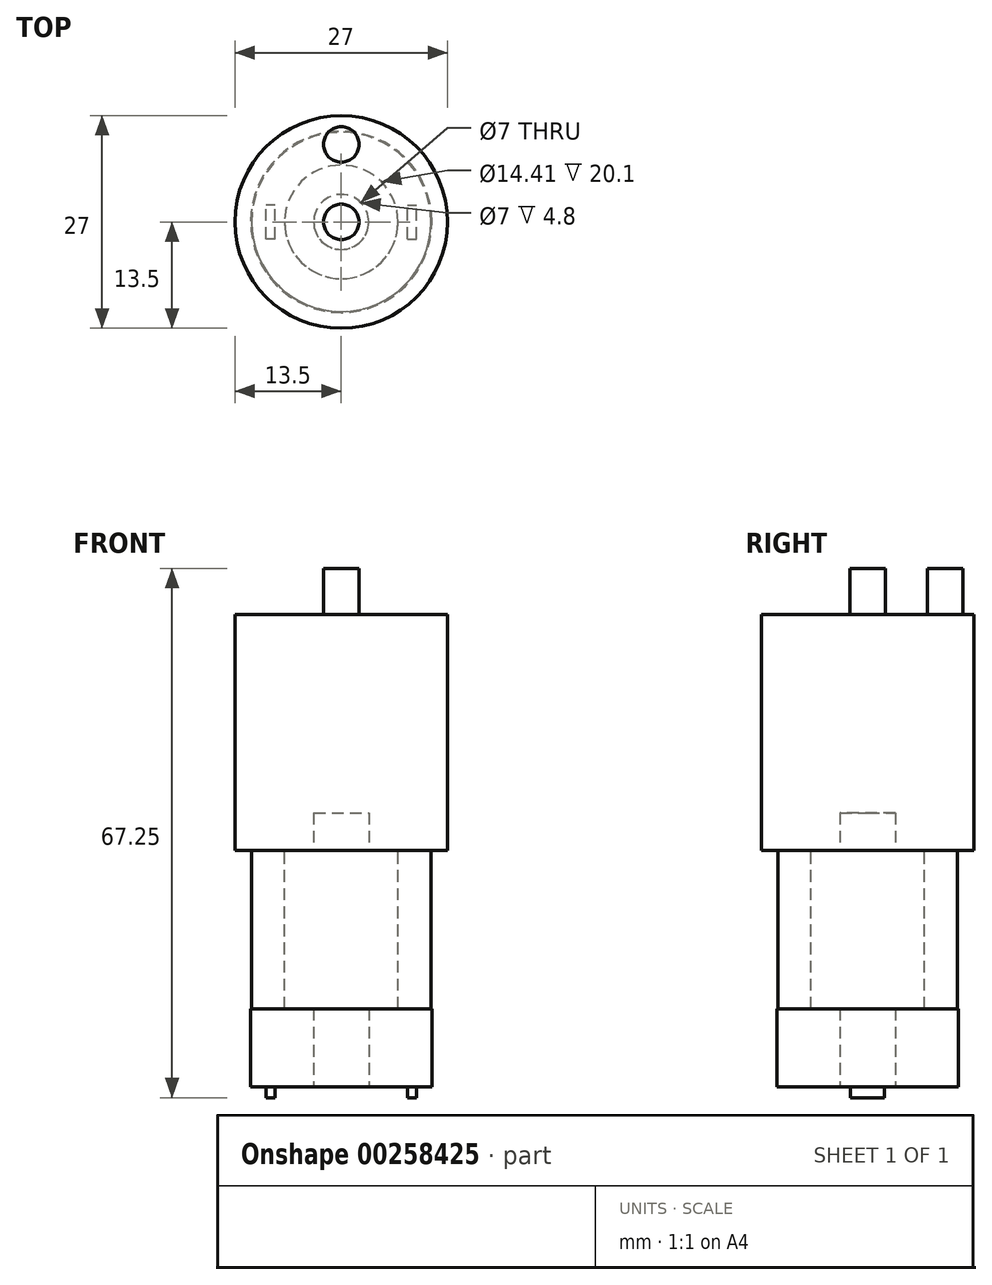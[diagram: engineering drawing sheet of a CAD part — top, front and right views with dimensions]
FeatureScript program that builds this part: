
annotation { "Feature Type Name" : "Feature", "Feature Type Description" : "" }
export const myFeature = defineFeature(function(context is Context, id is Id, definition is map)
    precondition{}
    {
        {
            var Q0;
            Q0=qCreatedBy(makeId("Right.planeOp"),FACE);
            var sketch = newSketch(context, id + "F0", { "sketchPlane" : qUnion([Q0])});
            skLineSegment(sketch, "E0", {"start": v(-11.4, 0) * mm, "end": v(-11.4, 30) * mm});
            skLineSegment(sketch, "E1", {"start": v(-11.4, 30) * mm, "end": v(-7.2, 30) * mm});
            skLineSegment(sketch, "E2", {"start": v(-7.2, 30) * mm, "end": v(-7.2, 0) * mm});
            skLineSegment(sketch, "E3", {"start": v(-7.2, 0) * mm, "end": v(-11.4, 0) * mm});
            skLineSegment(sketch, "E4", {"start": v(0, 33.61) * mm, "end": v(0, -7.5) * mm, "construction": true});
            skLineSegment(sketch, "E5", {"start": v(0, 0) * mm, "end": v(-11.4, 0) * mm, "construction": true});
            skSolve(sketch);
        }
        {
            var Q0;
            Q0=makeQuery(id+"F0.imprint","IMPRINT",FACE,{"disambiguationData":[TD([[makeQuery(id+"F0.imprint","IMPRINT",EDGE,{"derivedFrom":sQuery(id+"F0.wireOp",EDGE,"E0")}),-1.0]])]});
            var Q1;
            Q1=sQuery(id+"F0.wireOp",EDGE,"E4");
            revolve(context, id + "F1", {"entities" : qUnion([Q0]), "axis" : qUnion([Q1]), "revolveType" : RevolveType.FULL});
        }
        {
            var Q0;
            Q0=makeQuery(id+"F1.opRevolve","SWEPT_FACE",FACE,{"disambiguationData":[OSD([sQuery(id+"F0.wireOp",EDGE,"E1")])]});
            var sketch = newSketch(context, id + "F2", { "sketchPlane" : qUnion([Q0])});
            skCircle(sketch, "E6", {"center": v(0, 0) * mm, "radius": 13.5 * mm});
            skSolve(sketch);
        }
        {
            var Q0;
            Q0 = qSketchRegion(id + "F2", true);
            extrude(context, id + "F3", {"entities" : qUnion([Q0]), "operationType" : NewBodyOperationType.ADD, "depth" : 30 * mm});
        }
        {
            var Q0;
            Q0=makeQuery(id+"F1.opRevolve","SWEPT_FACE",FACE,{"disambiguationData":[OSD([sQuery(id+"F0.wireOp",EDGE,"E3")])]});
            var sketch = newSketch(context, id + "F4", { "sketchPlane" : qUnion([Q0])});
            skCircle(sketch, "E7", {"center": v(0, 0) * mm, "radius": 11.5 * mm});
            skSolve(sketch);
        }
        {
            var Q0;
            Q0 = qSketchRegion(id + "F4", true);
            extrude(context, id + "F5", {"entities" : qUnion([Q0]), "operationType" : NewBodyOperationType.ADD, "oppositeDirection" : true, "depth" : 9.9 * mm});
        }
        {
            var Q0;
            Q0=makeQuery(id+"F5.boolean.opBoolean","MERGE",FACE,{"derivedFrom":[makeQuery(id+"F1.opRevolve","SWEPT_FACE",FACE,{"disambiguationData":[OSD([sQuery(id+"F0.wireOp",EDGE,"E3")])]}),makeQuery(id+"F5.opExtrude","CAP_FACE",FACE,{"disambiguationData":[OSD([sQuery(id+"F4.wireOp",EDGE,"E7")])],"isStart":true})]});
            var sketch = newSketch(context, id + "F6", { "sketchPlane" : qUnion([Q0])});
            skCircle(sketch, "E8", {"center": v(0, 0) * mm, "radius": 3.5 * mm});
            skLineSegment(sketch, "E9.bottom", {"start": v(-8.42, 2.15) * mm, "end": v(-9.58, 2.15) * mm});
            skLineSegment(sketch, "E9.top", {"start": v(-8.42, -2.15) * mm, "end": v(-9.58, -2.15) * mm});
            skLineSegment(sketch, "E9.left", {"start": v(-8.42, 2.15) * mm, "end": v(-8.42, -2.15) * mm});
            skLineSegment(sketch, "E9.right", {"start": v(-9.58, 2.15) * mm, "end": v(-9.58, -2.15) * mm});
            skPoint(sketch, "E9.middle", {"position": v(-9, 0) * mm});
            skLineSegment(sketch, "E10", {"start": v(0, -12.15) * mm, "end": v(0, 12.15) * mm, "construction": true});
            skPoint(sketch, "E11.MirrorP", {"position": v(9, 0) * mm});
            skLineSegment(sketch, "E12.MirrorCS", {"start": v(9.58, 2.15) * mm, "end": v(9.58, -2.15) * mm});
            skLineSegment(sketch, "E13.MirrorCS", {"start": v(8.42, 2.15) * mm, "end": v(8.42, -2.15) * mm});
            skLineSegment(sketch, "E14.MirrorCS", {"start": v(8.42, -2.15) * mm, "end": v(9.58, -2.15) * mm});
            skLineSegment(sketch, "E15.MirrorCS", {"start": v(8.42, 2.15) * mm, "end": v(9.58, 2.15) * mm});
            skSolve(sketch);
        }
        {
            var Q0;
            Q0=makeQuery(id+"F6.imprint","IMPRINT",FACE,{"disambiguationData":[TD([[makeQuery(id+"F6.imprint","IMPRINT",EDGE,{"derivedFrom":sQuery(id+"F6.wireOp",EDGE,"E9.bottom")}),1.0]])]});
            var Q1;
            Q1=makeQuery(id+"F6.imprint","IMPRINT",FACE,{"disambiguationData":[TD([[makeQuery(id+"F6.imprint","IMPRINT",EDGE,{"derivedFrom":sQuery(id+"F6.wireOp",EDGE,"E12.MirrorCS")}),-1.0]])]});
            extrude(context, id + "F7", {"entities" : qUnion([Q0, Q1]), "operationType" : NewBodyOperationType.ADD, "depth" : 1.4 * mm});
        }
        {
            var Q0;
            Q0=makeQuery(id+"F6.imprint","IMPRINT",FACE,{"disambiguationData":[TD([[makeQuery(id+"F6.imprint","IMPRINT",EDGE,{"derivedFrom":sQuery(id+"F6.wireOp",EDGE,"E8")}),1.0]])]});
            var Q1;
            Q1=sQuery(id+"F6.wireOp",EDGE,"E8");
            extrude(context, id + "F8", {"entities" : qUnion([Q0]), "operationType" : NewBodyOperationType.REMOVE, "surfaceEntities" : qUnion([Q1]), "oppositeDirection" : true, "depth" : 34.8 * mm});
        }
        {
            var Q0;
            Q0=makeQuery(id+"F3.opExtrude","CAP_FACE",FACE,{"disambiguationData":[OSD([sQuery(id+"F2.wireOp",EDGE,"E6")])],"isStart":false});
            var sketch = newSketch(context, id + "F9", { "sketchPlane" : qUnion([Q0])});
            skCircle(sketch, "E16", {"center": v(0, 0) * mm, "radius": 2.25 * mm});
            skCircle(sketch, "E17", {"center": v(0, 9.85) * mm, "radius": 2.25 * mm});
            skLineSegment(sketch, "E18.bottom", {"start": v(13.5, 13.5) * mm, "end": v(-13.5, 13.5) * mm, "construction": true});
            skLineSegment(sketch, "E18.top", {"start": v(13.5, -13.5) * mm, "end": v(-13.5, -13.5) * mm, "construction": true});
            skLineSegment(sketch, "E18.left", {"start": v(13.5, 13.5) * mm, "end": v(13.5, -13.5) * mm, "construction": true});
            skLineSegment(sketch, "E18.right", {"start": v(-13.5, 13.5) * mm, "end": v(-13.5, -13.5) * mm, "construction": true});
            skSolve(sketch);
        }
        {
            var Q0;
            Q0=makeQuery(id+"F9.imprint","IMPRINT",FACE,{"disambiguationData":[TD([[makeQuery(id+"F9.imprint","IMPRINT",EDGE,{"derivedFrom":sQuery(id+"F9.wireOp",EDGE,"E16")}),1.0]])]});
            var Q1;
            Q1=makeQuery(id+"F9.imprint","IMPRINT",FACE,{"disambiguationData":[TD([[makeQuery(id+"F9.imprint","IMPRINT",EDGE,{"derivedFrom":sQuery(id+"F9.wireOp",EDGE,"E17")}),1.0]])]});
            extrude(context, id + "F10", {"entities" : qUnion([Q0, Q1]), "operationType" : NewBodyOperationType.ADD, "depth" : 5.85 * mm});
        }
    });
